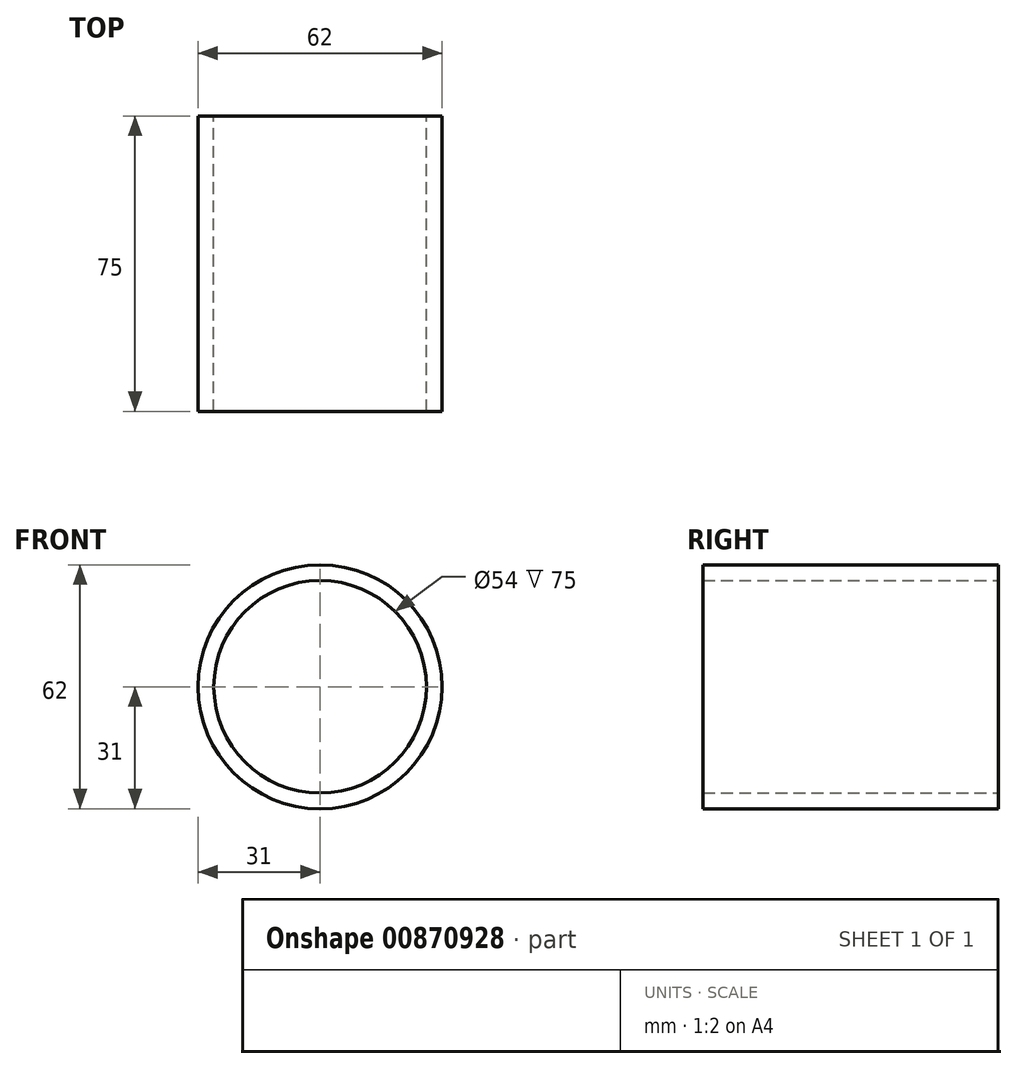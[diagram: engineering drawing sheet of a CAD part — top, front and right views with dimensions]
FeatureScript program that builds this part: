
annotation { "Feature Type Name" : "Feature", "Feature Type Description" : "" }
export const myFeature = defineFeature(function(context is Context, id is Id, definition is map)
    precondition{}
    {
        {
            var Q0;
            Q0=qCreatedBy(makeId("Front.planeOp"),FACE);
            var sketch = newSketch(context, id + "F0", { "sketchPlane" : qUnion([Q0])});
            skCircle(sketch, "E0", {"center": v(0, 0) * mm, "radius": 31 * mm});
            skCircle(sketch, "E1", {"center": v(0, 0) * mm, "radius": 27 * mm});
            skSolve(sketch);
        }
        {
            var Q0;
            Q0=makeQuery(id+"F0.imprint","IMPRINT",FACE,{"disambiguationData":[TD([[makeQuery(id+"F0.imprint","IMPRINT",EDGE,{"derivedFrom":sQuery(id+"F0.wireOp",EDGE,"E0")}),1.0]])]});
            extrude(context, id + "F1", {"entities" : qUnion([Q0]), "depth" : 75 * mm, "offsetDistance" : 25 * mm});
        }
    });
